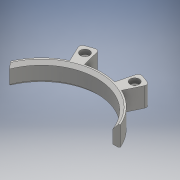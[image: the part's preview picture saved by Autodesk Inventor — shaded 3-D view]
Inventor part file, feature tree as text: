
AUTODESK INVENTOR PART (.ipt)
format: ipt  version: 2016 (Build 200138000, 138)  size: 190,976 bytes
history: native  units: mm
features: reference x6, hole x2, chamfer x2, other x1, extrude x1, sketch x1, fillet x1
ambient origin geometry x8: Origin, YZ Plane, XZ Plane, XY Plane, X Axis, Y Axis, Z Axis, Center Point
bodies: Solid1 (feature_tree)
feature tree (14):
  other  "Transmission.ipt"
  extrude  "Extrusion1"  Depth=10.0mm
  sketch  "Sketch2"  dims[d0=72.0mm d2=10.0mm d5=42.92mm d3=42.92mm d4=42.92mm d6=3.0mm d7=3.0mm d8=12.7mm d9=0.0mm d10=3.1mm d11=6.0mm d12=4.0mm d13=2.0mm d14=90.0deg d15=8.0mm d16=20.594885mm d17=2.0mm d18=2.0mm d19=45.0deg d20=2.0mm d21=2.0mm d22=45.0deg d23=6.0mm d24=6.0mm d25=4.0mm d26=2.0mm d27=90.0deg d28=3.0mm d29=0.0mm d33=3.0mm d34=4.5mm d35=4.5mm d36=4.5mm d37=4.5mm d38=2.0mm]
  hole  "Hole1"  [1 undecoded]
  hole  "Hole2"  [1 undecoded]
  chamfer  "Chamfer1"  Distance=42.92mm
  chamfer  "Chamfer2"  Distance=3.0mm
  fillet  "Fillet1"  Radius=3.0mm
  reference  "Reference1"
  reference  "Reference2"
  reference  "Reference3"
  reference  "Reference4"
  reference  "Reference5"
  reference  "Reference6"
note: 2 required parameter values undecoded (feature->parameter linkage not recoverable at this tier; creation-order binding heuristic only, values carry confidence <= 0.55)
